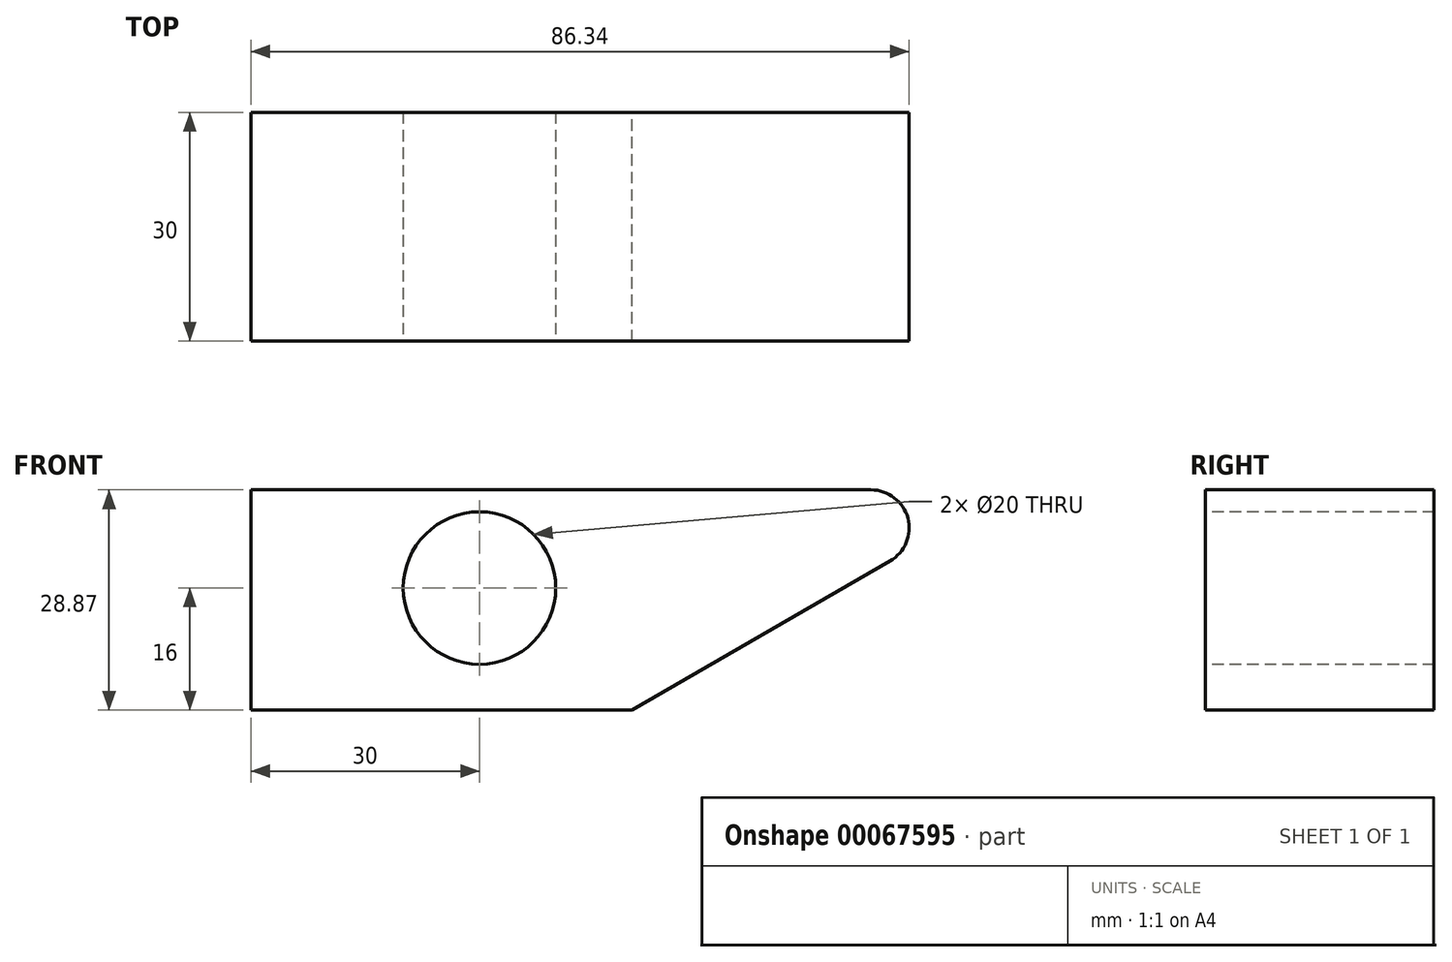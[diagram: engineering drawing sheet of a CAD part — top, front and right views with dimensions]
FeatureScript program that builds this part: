
annotation { "Feature Type Name" : "Feature", "Feature Type Description" : "" }
export const myFeature = defineFeature(function(context is Context, id is Id, definition is map)
    precondition{}
    {
        {
            var Q0;
            Q0=qCreatedBy(makeId("Front.planeOp"),FACE);
            var sketch = newSketch(context, id + "F0", { "sketchPlane" : qUnion([Q0])});
            skLineSegment(sketch, "E0", {"start": v(0, 0) * mm, "end": v(50, 0) * mm});
            skLineSegment(sketch, "E1", {"start": v(50, 0) * mm, "end": v(100, 28.87) * mm});
            skLineSegment(sketch, "E2", {"start": v(100, 28.87) * mm, "end": v(0, 28.87) * mm});
            skLineSegment(sketch, "E3", {"start": v(0, 28.87) * mm, "end": v(0, 0) * mm});
            skSolve(sketch);
        }
        {
            var Q0;
            Q0 = qSketchRegion(id + "F0", true);
            extrude(context, id + "F1", {"entities" : qUnion([Q0]), "depth" : 30 * mm});
        }
        {
            var Q0;
            Q0=makeQuery(id+"F1.opExtrude","CAP_FACE",FACE,{"disambiguationData":[OSD([sQuery(id+"F0.wireOp",EDGE,"E0"),sQuery(id+"F0.wireOp",EDGE,"E1"),sQuery(id+"F0.wireOp",EDGE,"E2"),sQuery(id+"F0.wireOp",EDGE,"E3")])],"isStart":false});
            var sketch = newSketch(context, id + "F2", { "sketchPlane" : qUnion([Q0])});
            skCircle(sketch, "E4", {"center": v(30, 16) * mm, "radius": 10 * mm});
            skSolve(sketch);
        }
        {
            var Q0;
            Q0 = qSketchRegion(id + "F2", true);
            var Q1;
            Q1=makeQuery(id+"F1.opExtrude","CAP_FACE",FACE,{"disambiguationData":[OSD([sQuery(id+"F0.wireOp",EDGE,"E0"),sQuery(id+"F0.wireOp",EDGE,"E1"),sQuery(id+"F0.wireOp",EDGE,"E2"),sQuery(id+"F0.wireOp",EDGE,"E3")])],"isStart":true});
            extrude(context, id + "F3", {"entities" : qUnion([Q0]), "operationType" : NewBodyOperationType.REMOVE, "endBound" : BoundingType.UP_TO_SURFACE, "oppositeDirection" : true, "endBoundEntityFace" : qUnion([Q1]), "depth" : 67.93 * mm});
        }
        {
            var Q0;
            Q0=makeQuery(id+"F1.opExtrude","SWEPT_EDGE",EDGE,{"disambiguationData":[OSD([sQuery(id+"F0.wireOp",EDGE,"E1"),sQuery(id+"F0.wireOp",EDGE,"E2")])]});
            fillet(context, id + "F4", {"entities" : qUnion([Q0]), "radius" : 5 * mm, "tangentPropagation" : true, "allowEdgeOverflow" : false});
        }
    });
